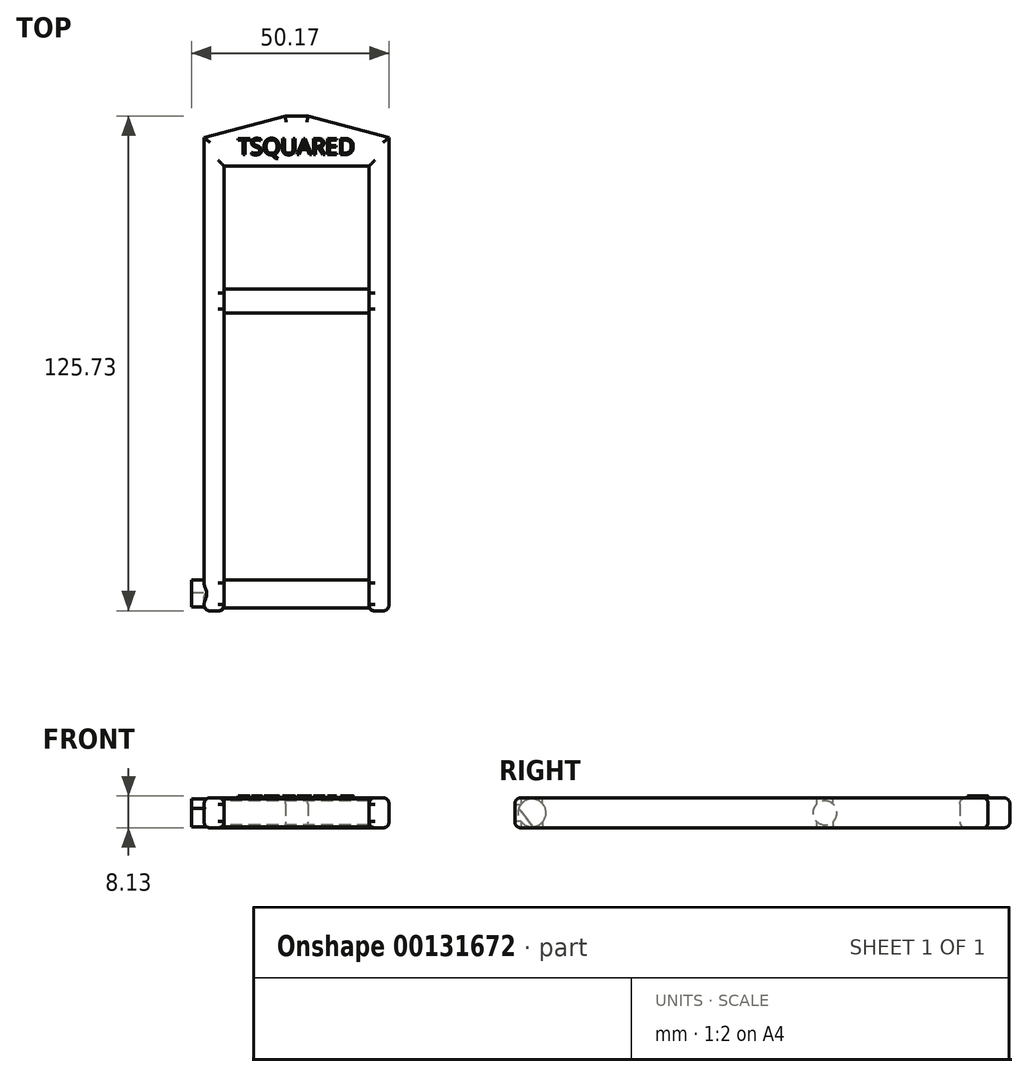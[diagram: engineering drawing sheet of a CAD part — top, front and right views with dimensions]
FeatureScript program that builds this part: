
annotation { "Feature Type Name" : "Feature", "Feature Type Description" : "" }
export const myFeature = defineFeature(function(context is Context, id is Id, definition is map)
    precondition{}
    {
        {
            var Q0;
            Q0=qCreatedBy(makeId("Top.planeOp"),FACE);
            var sketch = newSketch(context, id + "F0", { "sketchPlane" : qUnion([Q0])});
            skLineSegment(sketch, "E0", {"start": v(0, 0) * mm, "end": v(0, 120.2) * mm});
            skLineSegment(sketch, "E1", {"start": v(20.64, 125.73) * mm, "end": v(26.35, 125.73) * mm});
            skLineSegment(sketch, "E2", {"start": v(47, 120.2) * mm, "end": v(47, 0) * mm});
            skLineSegment(sketch, "E3", {"start": v(47, 0) * mm, "end": v(41.91, 0) * mm});
            skLineSegment(sketch, "E4", {"start": v(41.91, 0) * mm, "end": v(41.91, 113.03) * mm});
            skLineSegment(sketch, "E5", {"start": v(41.91, 113.03) * mm, "end": v(5.08, 113.03) * mm});
            skLineSegment(sketch, "E6", {"start": v(5.08, 113.03) * mm, "end": v(5.08, 0) * mm});
            skLineSegment(sketch, "E7", {"start": v(5.08, 0) * mm, "end": v(0, 0) * mm});
            skLineSegment(sketch, "E8", {"start": v(20.64, 125.73) * mm, "end": v(0, 120.2) * mm});
            skLineSegment(sketch, "E9", {"start": v(26.35, 125.73) * mm, "end": v(47, 120.2) * mm});
            skSolve(sketch);
        }
        {
            var Q0;
            Q0 = qSketchRegion(id + "F0", true);
            extrude(context, id + "F1", {"entities" : qUnion([Q0]), "depth" : 7.62 * mm});
        }
        {
            var Q0;
            Q0=makeQuery(id+"F1.opExtrude","SWEPT_FACE",FACE,{"disambiguationData":[OSD([sQuery(id+"F0.wireOp",EDGE,"E6")])]});
            var sketch = newSketch(context, id + "F2", { "sketchPlane" : qUnion([Q0])});
            skCircle(sketch, "E10", {"center": v(78.74, 3.81) * mm, "radius": 3.05 * mm});
            skPoint(sketch, "E10.centerSnap0", {"position": v(113.03, 3.81) * mm});
            skSolve(sketch);
        }
        {
            var Q0;
            Q0 = qSketchRegion(id + "F2", true);
            extrude(context, id + "F3", {"entities" : qUnion([Q0]), "operationType" : NewBodyOperationType.ADD, "endBound" : BoundingType.UP_TO_NEXT, "depth" : 25.4 * mm});
        }
        {
            var Q0;
            Q0=makeQuery(id+"F1.opExtrude","SWEPT_FACE",FACE,{"disambiguationData":[OSD([sQuery(id+"F0.wireOp",EDGE,"E6")])]});
            var sketch = newSketch(context, id + "F4", { "sketchPlane" : qUnion([Q0])});
            skCircle(sketch, "E11", {"center": v(4.32, 3.81) * mm, "radius": 3.56 * mm});
            skPoint(sketch, "E11.centerSnap0", {"position": v(0, 3.81) * mm});
            skSolve(sketch);
        }
        {
            var Q0;
            Q0 = qSketchRegion(id + "F4", true);
            extrude(context, id + "F5", {"entities" : qUnion([Q0]), "operationType" : NewBodyOperationType.ADD, "endBound" : BoundingType.UP_TO_NEXT, "depth" : 25.4 * mm});
        }
        {
            var Q0;
            Q0=makeQuery(id+"F1.opExtrude","CAP_FACE",FACE,{"disambiguationData":[OSD([sQuery(id+"F0.wireOp",EDGE,"E0"),sQuery(id+"F0.wireOp",EDGE,"E1"),sQuery(id+"F0.wireOp",EDGE,"E2"),sQuery(id+"F0.wireOp",EDGE,"E3"),sQuery(id+"F0.wireOp",EDGE,"E4"),sQuery(id+"F0.wireOp",EDGE,"E5"),sQuery(id+"F0.wireOp",EDGE,"E6"),sQuery(id+"F0.wireOp",EDGE,"E7"),sQuery(id+"F0.wireOp",EDGE,"E8"),sQuery(id+"F0.wireOp",EDGE,"E9")])],"isStart":false});
            var Q1;
            Q1=makeQuery(id+"F1.opExtrude","CAP_FACE",FACE,{"disambiguationData":[OSD([sQuery(id+"F0.wireOp",EDGE,"E0"),sQuery(id+"F0.wireOp",EDGE,"E1"),sQuery(id+"F0.wireOp",EDGE,"E2"),sQuery(id+"F0.wireOp",EDGE,"E3"),sQuery(id+"F0.wireOp",EDGE,"E4"),sQuery(id+"F0.wireOp",EDGE,"E5"),sQuery(id+"F0.wireOp",EDGE,"E6"),sQuery(id+"F0.wireOp",EDGE,"E7"),sQuery(id+"F0.wireOp",EDGE,"E8"),sQuery(id+"F0.wireOp",EDGE,"E9")])],"isStart":true});
            var Q2;
            Q2=makeQuery(id+"F1.opExtrude","SWEPT_FACE",FACE,{"disambiguationData":[OSD([sQuery(id+"F0.wireOp",EDGE,"E3")])]});
            var Q3;
            Q3=makeQuery(id+"F1.opExtrude","SWEPT_FACE",FACE,{"disambiguationData":[OSD([sQuery(id+"F0.wireOp",EDGE,"E7")])]});
            fillet(context, id + "F6", {"entities" : qUnion([Q0, Q1, Q2, Q3]), "radius" : 1.52 * mm, "tangentPropagation" : true, "allowEdgeOverflow" : false});
        }
        {
            var Q0;
            Q0=makeQuery(id+"F1.opExtrude","CAP_FACE",FACE,{"disambiguationData":[OSD([sQuery(id+"F0.wireOp",EDGE,"E0"),sQuery(id+"F0.wireOp",EDGE,"E1"),sQuery(id+"F0.wireOp",EDGE,"E2"),sQuery(id+"F0.wireOp",EDGE,"E3"),sQuery(id+"F0.wireOp",EDGE,"E4"),sQuery(id+"F0.wireOp",EDGE,"E5"),sQuery(id+"F0.wireOp",EDGE,"E6"),sQuery(id+"F0.wireOp",EDGE,"E7"),sQuery(id+"F0.wireOp",EDGE,"E8"),sQuery(id+"F0.wireOp",EDGE,"E9")])],"isStart":false});
            var sketch = newSketch(context, id + "F7", { "sketchPlane" : qUnion([Q0])});
            skText(sketch, "E12", { "text": "TSQUARED", "fontName": "OpenSans-Regular.ttf"});
            const initialGuessF7  = {"E12": [0.00853, 0.1159, 1, 0, 0.00416]};
            skSetInitialGuess(sketch, initialGuessF7);
            skSolve(sketch);
        }
        {
            var Q0;
            Q0 = qSketchRegion(id + "F7", true);
            extrude(context, id + "F8", {"entities" : qUnion([Q0]), "operationType" : NewBodyOperationType.ADD, "depth" : 0.5 * mm});
        }
        {
            var Q0;
            Q0=makeQuery(id+"F1.opExtrude","SWEPT_FACE",FACE,{"disambiguationData":[OSD([sQuery(id+"F0.wireOp",EDGE,"E0")])]});
            var sketch = newSketch(context, id + "F9", { "sketchPlane" : qUnion([Q0])});
            skArc(sketch, "E13", {"start": v(-0.96, 4.97) * mm, "mid": v(-7.12, 6) * mm, "end": v(-4.63, 0.27) * mm});
            skLineSegment(sketch, "E14", {"start": v(-4.63, 0.27) * mm, "end": v(-0.96, 4.97) * mm});
            skSolve(sketch);
        }
        {
            var Q0;
            Q0 = qSketchRegion(id + "F9", true);
            extrude(context, id + "F10", {"entities" : qUnion([Q0]), "operationType" : NewBodyOperationType.ADD, "depth" : 3.17 * mm, "hasSecondDirection" : true, "secondDirectionBound" : SecondDirectionBoundingType.UP_TO_NEXT, "secondDirectionOppositeDirection" : true, "secondDirectionDepth" : 25.4 * mm});
        }
        {
            var Q0;
            Q0=qCreatedBy(makeId("Right.planeOp"),FACE);
            cPlane(context, id + "F11", {"entities" : qUnion([Q0]), "cplaneType" : CPlaneType.OFFSET, "offset" : 23.5 * mm, "width" : 152.4 * mm, "height" : 152.4 * mm});
        }
    });
